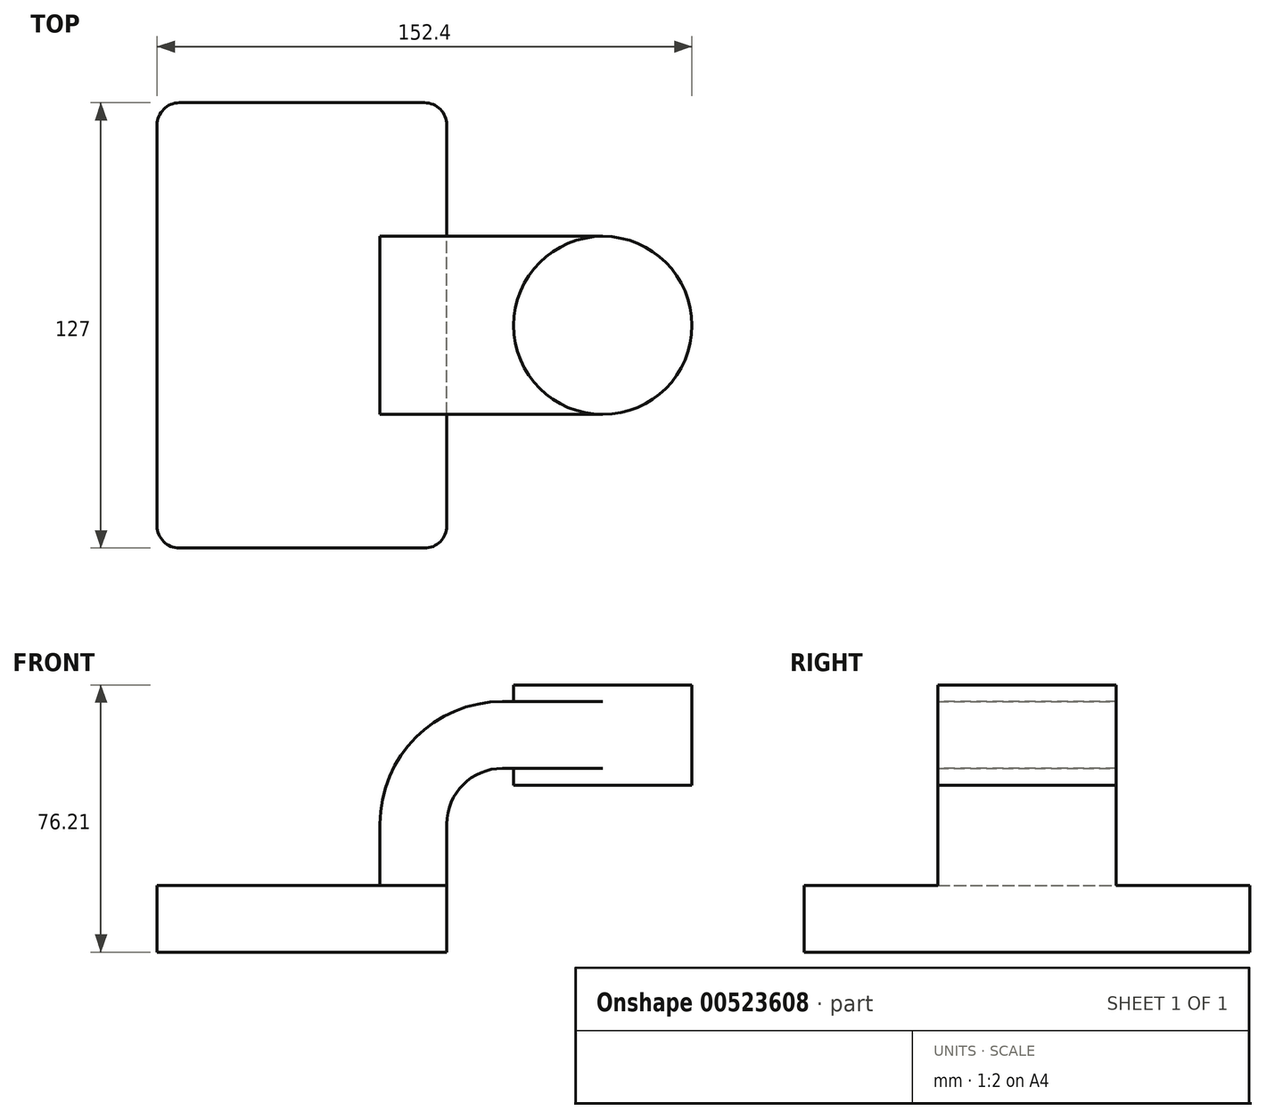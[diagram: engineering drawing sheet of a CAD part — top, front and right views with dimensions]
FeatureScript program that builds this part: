
annotation { "Feature Type Name" : "Feature", "Feature Type Description" : "" }
export const myFeature = defineFeature(function(context is Context, id is Id, definition is map)
    precondition{}
    {
        {
            var Q0;
            Q0=qCreatedBy(makeId("Front.planeOp"),FACE);
            var sketch = newSketch(context, id + "F0", { "sketchPlane" : qUnion([Q0])});
            skLineSegment(sketch, "E0.bottom", {"start": v(41.27, 9.53) * mm, "end": v(-41.28, 9.53) * mm});
            skLineSegment(sketch, "E0.top", {"start": v(41.28, -9.52) * mm, "end": v(-41.27, -9.52) * mm});
            skLineSegment(sketch, "E0.left", {"start": v(41.28, 9.53) * mm, "end": v(41.28, -9.52) * mm});
            skLineSegment(sketch, "E0.right", {"start": v(-41.28, 9.53) * mm, "end": v(-41.27, -9.52) * mm});
            skPoint(sketch, "E0.middle", {"position": v(0, 0) * mm});
            skLineSegment(sketch, "E1.bottom", {"start": v(111.12, 66.68) * mm, "end": v(60.32, 66.68) * mm});
            skLineSegment(sketch, "E1.top", {"start": v(111.12, 38.1) * mm, "end": v(60.33, 38.1) * mm});
            skLineSegment(sketch, "E1.left", {"start": v(111.12, 66.68) * mm, "end": v(111.12, 38.1) * mm});
            skLineSegment(sketch, "E1.right", {"start": v(60.32, 66.68) * mm, "end": v(60.33, 38.1) * mm});
            skPoint(sketch, "E1.middle", {"position": v(85.73, 52.39) * mm});
            skLineSegment(sketch, "E2", {"start": v(41.27, 9.53) * mm, "end": v(41.27, 27) * mm});
            skArc(sketch, "E3", {"start": v(41.27, 27) * mm, "mid": v(45.92, 38.23) * mm, "end": v(57.15, 42.88) * mm});
            skLineSegment(sketch, "E4", {"start": v(57.15, 42.88) * mm, "end": v(85.72, 42.88) * mm});
            skLineSegment(sketch, "E5.0", {"start": v(57.15, 61.93) * mm, "end": v(85.72, 61.93) * mm});
            skArc(sketch, "E5.1", {"start": v(22.23, 27) * mm, "mid": v(32.45, 51.7) * mm, "end": v(57.15, 61.93) * mm});
            skLineSegment(sketch, "E5.2", {"start": v(22.22, 9.53) * mm, "end": v(22.22, 27) * mm});
            skFitSpline(sketch, "E6", {"points": [v(-41.28, 9.53) * mm, v(57.15, 61.93) * mm], "startDerivative": vector(0, 44.91) * mm, "endDerivative": vector(171.45, 0) * mm});
            skLineSegment(sketch, "E7", {"start": v(85.72, 66.68) * mm, "end": v(85.72, 38.1) * mm});
            skSolve(sketch);
        }
        {
            var Q0;
            Q0=makeQuery(id+"F0.imprint","IMPRINT",FACE,{"disambiguationData":[TD([[makeQuery(id+"F0.imprint","IMPRINT",EDGE,{"derivedFrom":sQuery(id+"F0.wireOp",EDGE,"E0.top")}),-1.0]])]});
            extrude(context, id + "F1", {"entities" : qUnion([Q0]), "endBound" : BoundingType.SYMMETRIC, "depth" : 127 * mm, "offsetDistance" : 25.4 * mm});
        }
        {
            var Q0;
            {var subQ0=sQuery(id+"F0.wireOp",EDGE,"E5.0");var subQ1=sQuery(id+"F0.wireOp",EDGE,"E1.right");var subQ2=makeQuery(id+"F0.imprint","INTERSECT",VERTEX,{"derivedFrom":[subQ1,subQ0]});Q0=makeQuery(id+"F0.imprint","IMPRINT",FACE,{"disambiguationData":[TD([[makeQuery(id+"F0.imprint","IMPRINT",EDGE,{"disambiguationData":[TD([[subQ2,-1.0]])],"derivedFrom":subQ1}),1.0]])]});}
            var Q1;
            {var subQ1=sQuery(id+"F0.wireOp",EDGE,"E2");Q1=makeQuery(id+"F0.imprint","IMPRINT",FACE,{"disambiguationData":[TD([[makeQuery(id+"F0.imprint","IMPRINT",EDGE,{"derivedFrom":subQ1}),1.0]])]});}
            extrude(context, id + "F2", {"entities" : qUnion([Q0, Q1]), "operationType" : NewBodyOperationType.ADD, "endBound" : BoundingType.SYMMETRIC, "depth" : 50.8 * mm, "offsetDistance" : 25.4 * mm});
        }
        {
            var Q0;
            Q0=makeQuery(id+"F0.imprint","IMPRINT",FACE,{"disambiguationData":[TD([[makeQuery(id+"F0.imprint","IMPRINT",EDGE,{"derivedFrom":sQuery(id+"F0.wireOp",EDGE,"E5.1")}),1.0]])]});
            extrude(context, id + "F3", {"entities" : qUnion([Q0]), "operationType" : NewBodyOperationType.ADD, "endBound" : BoundingType.SYMMETRIC, "depth" : 15.88 * mm, "offsetDistance" : 25.4 * mm});
        }
        {
            var Q0;
            {var subQ0=sQuery(id+"F0.wireOp",EDGE,"E1.left");Q0=makeQuery(id+"F0.imprint","IMPRINT",FACE,{"disambiguationData":[TD([[makeQuery(id+"F0.imprint","IMPRINT",EDGE,{"derivedFrom":subQ0}),-1.0]])]});}
            var Q1;
            Q1=sQuery(id+"F0.wireOp",EDGE,"E7");
            revolve(context, id + "F4", {"operationType" : NewBodyOperationType.ADD, "entities" : qUnion([Q0]), "axis" : qUnion([Q1]), "revolveType" : RevolveType.FULL});
        }
        {
            var Q0;
            Q0=makeQuery(id+"F1.opExtrude","CAP_EDGE",EDGE,{"disambiguationData":[OSD([sQuery(id+"F0.wireOp",EDGE,"E0.right")])],"isStart":false});
            var Q1;
            Q1=makeQuery(id+"F1.opExtrude","CAP_EDGE",EDGE,{"disambiguationData":[OSD([sQuery(id+"F0.wireOp",EDGE,"E0.left")])],"isStart":false});
            var Q2;
            Q2=makeQuery(id+"F1.opExtrude","CAP_EDGE",EDGE,{"disambiguationData":[OSD([sQuery(id+"F0.wireOp",EDGE,"E0.left")])],"isStart":true});
            var Q3;
            Q3=makeQuery(id+"F1.opExtrude","CAP_EDGE",EDGE,{"disambiguationData":[OSD([sQuery(id+"F0.wireOp",EDGE,"E0.right")])],"isStart":true});
            fillet(context, id + "F5", {"entities" : qUnion([Q0, Q1, Q2, Q3]), "radius" : 6.35 * mm, "tangentPropagation" : true, "allowEdgeOverflow" : false});
        }
    });
